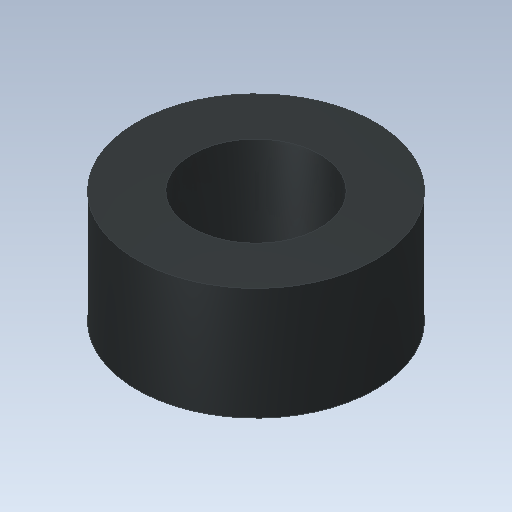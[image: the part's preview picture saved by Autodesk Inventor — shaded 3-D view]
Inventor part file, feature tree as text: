
AUTODESK INVENTOR PART (.ipt)
format: ipt  version: 2020 (Build 240168000, 168)  size: 99,328 bytes
history: native  units: mm
features: other x1, extrude x1, sketch x1
ambient origin geometry x8: Origin, YZ Plane, XZ Plane, XY Plane, X Axis, Y Axis, Z Axis, Center Point
bodies: Body1 (feature_tree)
feature tree (3):
  other  "Bryła1"
  extrude  "Wyciągnięcie proste1"  Depth=28.0mm
  sketch  "Szkic1"
